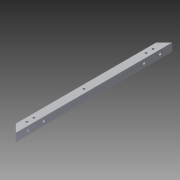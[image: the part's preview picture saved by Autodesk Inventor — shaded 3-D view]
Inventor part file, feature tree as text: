
AUTODESK INVENTOR PART (.ipt)
format: ipt  version: 2014 SP1 (Build 180222100, 222)  size: 117,248 bytes
history: native  units: in
note: dims shown in document units (in); Inventor stores cm internally (conversion verified against a paired STEP export)
features: reference x9, extrude x4, sketch x4
ambient origin geometry x8: Origin, YZ Plane, XZ Plane, XY Plane, X Axis, Y Axis, Z Axis, Center Point
bodies: Solid1 (feature_tree)
feature tree (17):
  extrude  "Extrusion1"  Depth=1.0in
  extrude  "Extrusion2"  Depth=0.0625in TaperAngle=0.0deg
  extrude  "Extrusion3"  TaperAngle=45.0deg  [1 undecoded]
  extrude  "Extrusion4"  Depth=1.0in TaperAngle=0.0deg
  sketch  "Sketch1"  dims[d0=1.0in d2=1.0in]
  sketch  "Sketch2"  dims[d3=0.0625in d4=19.5in d5=0.0in]
  sketch  "Sketch3"  dims[d6=135.0deg d7=45.0deg]
  reference  "Reference1"
  reference  "Reference2"
  reference  "Reference3"
  reference  "Reference4"
  sketch  "Sketch4"  dims[d8=19.5in d9=0.0in d10=1.0in d11=0.0in d12=1.0in d13=0.0in]
  reference  "Reference5"
  reference  "Reference6"
  reference  "Reference7"
  reference  "Reference8"
  reference  "Reference9"
note: 1 required parameter value undecoded (feature->parameter linkage not recoverable at this tier; creation-order binding heuristic only, values carry confidence <= 0.55)
